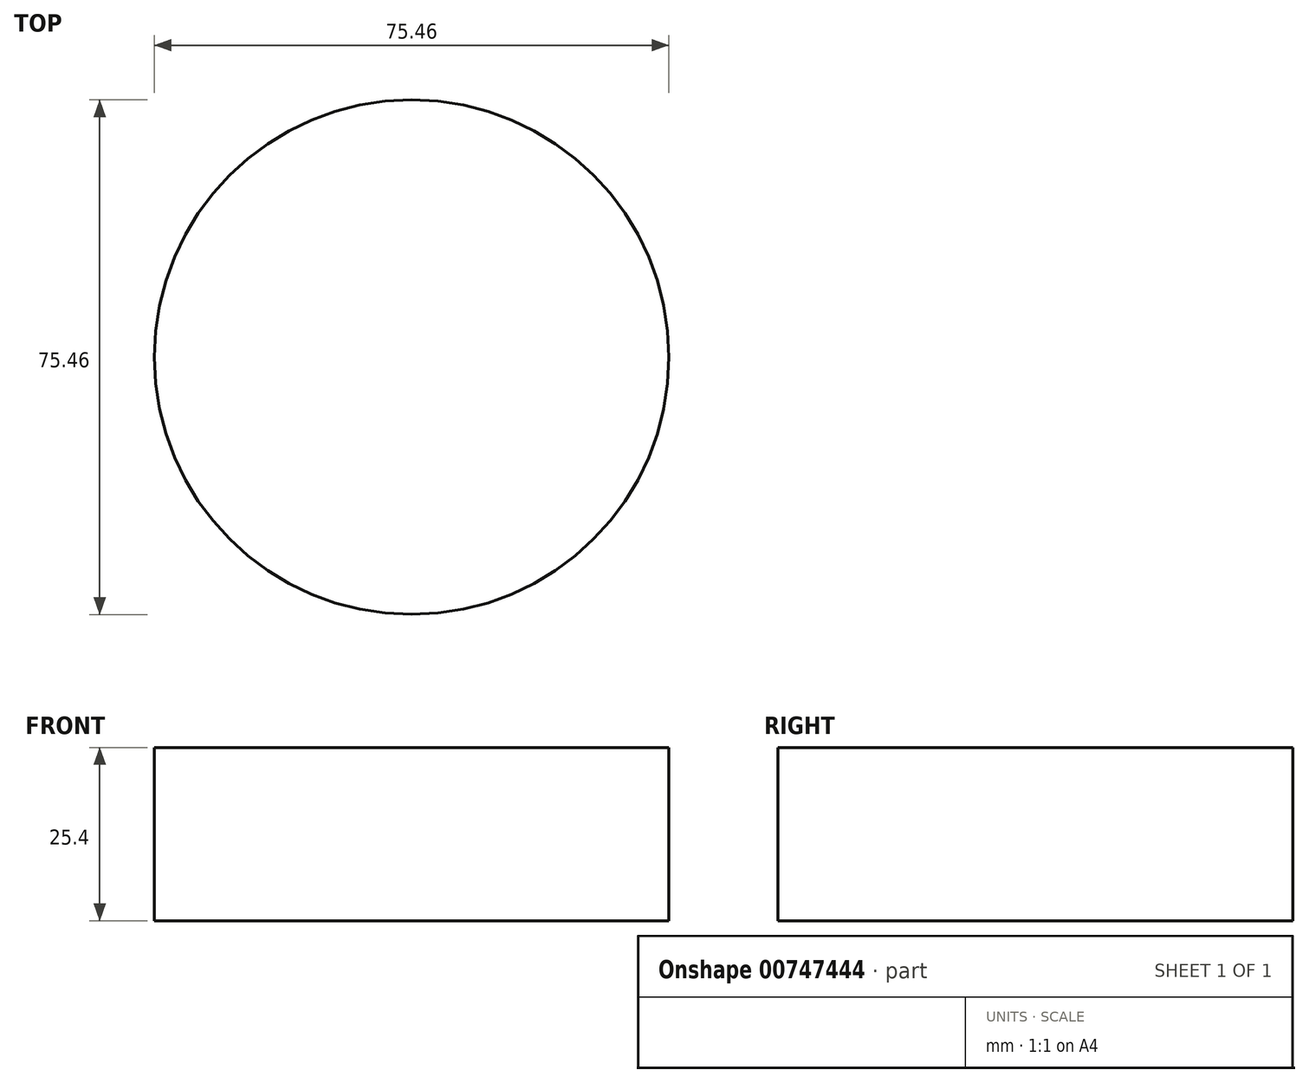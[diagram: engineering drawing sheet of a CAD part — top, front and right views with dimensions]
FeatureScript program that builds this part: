
annotation { "Feature Type Name" : "Feature", "Feature Type Description" : "" }
export const myFeature = defineFeature(function(context is Context, id is Id, definition is map)
    precondition{}
    {
        {
            var Q0;
            Q0=qCreatedBy(makeId("Top.planeOp"),FACE);
            var sketch = newSketch(context, id + "F0", { "sketchPlane" : qUnion([Q0])});
            skCircle(sketch, "E0", {"center": v(0, 0) * mm, "radius": 30.93 * mm});
            skCircle(sketch, "E1", {"center": v(0, 0) * mm, "radius": 37.73 * mm});
            skSolve(sketch);
        }
        {
            var Q0;
            Q0=makeQuery(id+"F0.imprint","IMPRINT",FACE,{"disambiguationData":[TD([[makeQuery(id+"F0.imprint","IMPRINT",EDGE,{"derivedFrom":sQuery(id+"F0.wireOp",EDGE,"E0")}),1.0]])]});
            var Q1;
            Q1=makeQuery(id+"F0.imprint","IMPRINT",FACE,{"disambiguationData":[TD([[makeQuery(id+"F0.imprint","IMPRINT",EDGE,{"derivedFrom":sQuery(id+"F0.wireOp",EDGE,"E0")}),-1.0]])]});
            extrude(context, id + "F1", {"entities" : qUnion([Q0, Q1]), "depth" : 25.4 * mm, "offsetDistance" : 25.4 * mm});
        }
    });
